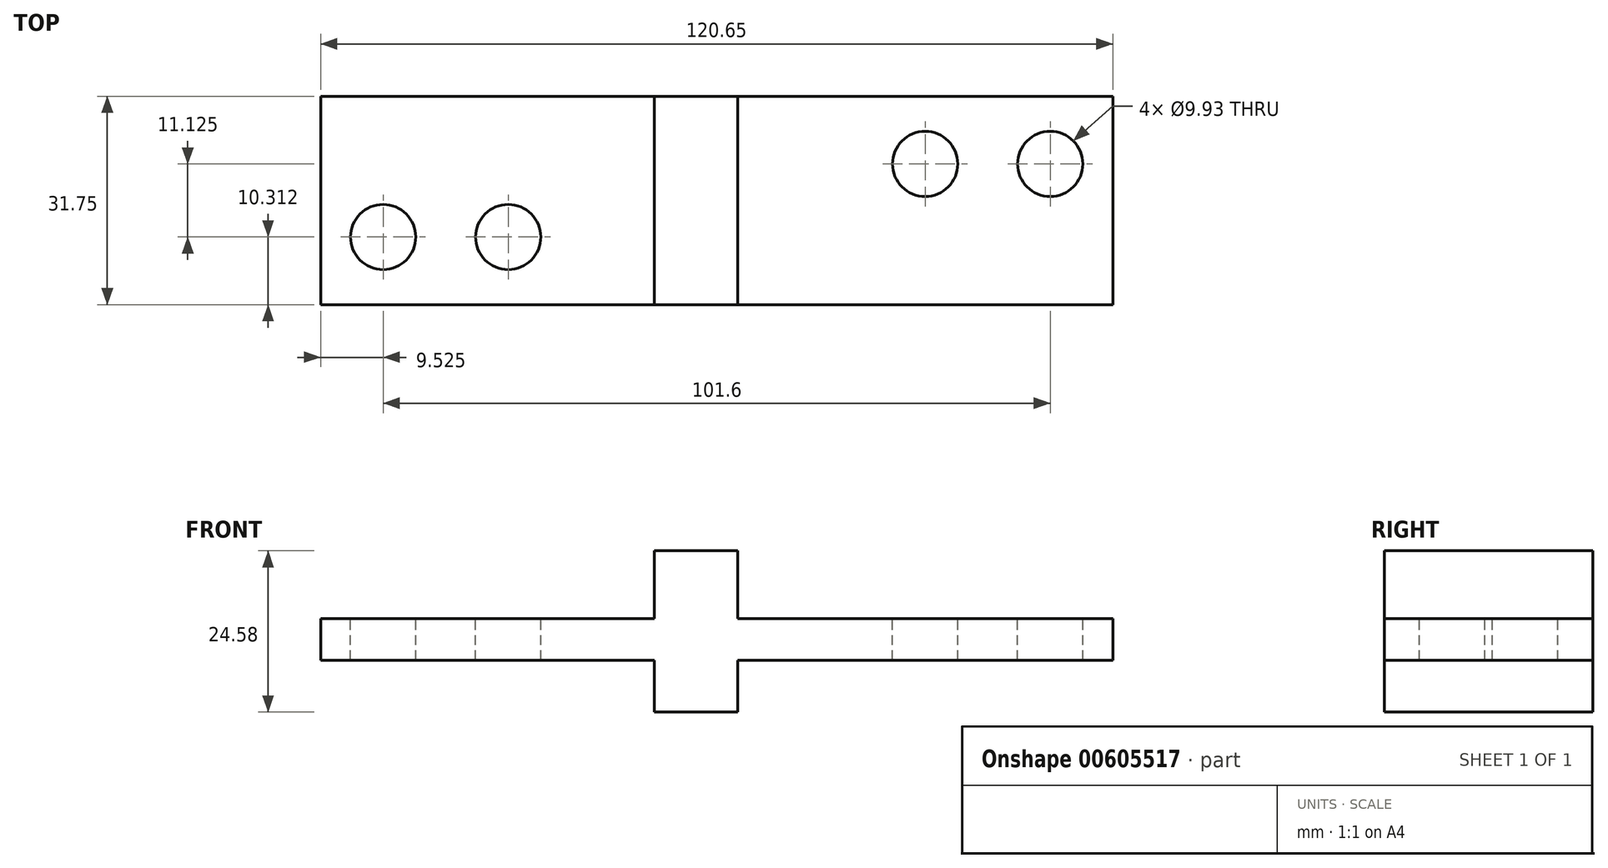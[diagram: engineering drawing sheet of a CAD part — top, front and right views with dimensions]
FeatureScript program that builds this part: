
annotation { "Feature Type Name" : "Feature", "Feature Type Description" : "" }
export const myFeature = defineFeature(function(context is Context, id is Id, definition is map)
    precondition{}
    {
        {
            var Q0;
            Q0=qCreatedBy(makeId("Front.planeOp"),FACE);
            var sketch = newSketch(context, id + "F0", { "sketchPlane" : qUnion([Q0])});
            skLineSegment(sketch, "E0", {"start": v(0, 0) * mm, "end": v(50.8, 0) * mm});
            skLineSegment(sketch, "E1", {"start": v(50.8, 0) * mm, "end": v(50.8, -7.92) * mm});
            skLineSegment(sketch, "E2", {"start": v(50.8, -7.92) * mm, "end": v(63.5, -7.92) * mm});
            skLineSegment(sketch, "E3", {"start": v(63.5, -7.92) * mm, "end": v(63.5, 0) * mm});
            skLineSegment(sketch, "E4", {"start": v(63.5, 0) * mm, "end": v(120.65, 0) * mm});
            skLineSegment(sketch, "E5", {"start": v(120.65, 0) * mm, "end": v(120.65, 6.35) * mm});
            skLineSegment(sketch, "E6", {"start": v(120.65, 6.35) * mm, "end": v(63.5, 6.35) * mm});
            skLineSegment(sketch, "E7", {"start": v(63.5, 6.35) * mm, "end": v(63.5, 16.66) * mm});
            skLineSegment(sketch, "E8", {"start": v(63.5, 16.66) * mm, "end": v(50.8, 16.66) * mm});
            skLineSegment(sketch, "E9", {"start": v(50.8, 16.66) * mm, "end": v(50.8, 6.35) * mm});
            skLineSegment(sketch, "E10", {"start": v(50.8, 6.35) * mm, "end": v(0, 6.35) * mm});
            skLineSegment(sketch, "E11", {"start": v(0, 6.35) * mm, "end": v(0, 0) * mm});
            skSolve(sketch);
        }
        {
            var Q0;
            Q0=makeQuery(id+"F0.imprint","IMPRINT",FACE,{"disambiguationData":[TD([[makeQuery(id+"F0.imprint","IMPRINT",EDGE,{"derivedFrom":sQuery(id+"F0.wireOp",EDGE,"E0")}),1.0]])]});
            extrude(context, id + "F1", {"entities" : qUnion([Q0]), "depth" : 31.75 * mm, "offsetDistance" : 25.4 * mm});
        }
        {
            var Q0;
            Q0=qCreatedBy(makeId("Top.planeOp"),FACE);
            var sketch = newSketch(context, id + "F2", { "sketchPlane" : qUnion([Q0])});
            skCircle(sketch, "E12", {"center": v(9.53, -21.44) * mm, "radius": 4.97 * mm});
            skCircle(sketch, "E13", {"center": v(28.57, -21.44) * mm, "radius": 4.97 * mm});
            skCircle(sketch, "E14", {"center": v(92.08, -10.31) * mm, "radius": 4.97 * mm});
            skCircle(sketch, "E15", {"center": v(111.12, -10.31) * mm, "radius": 4.97 * mm});
            skSolve(sketch);
        }
        {
            var Q0;
            Q0=sQuery(id+"F2.wireOp",VERTEX,"E15.center");
            var Q1;
            Q1=sQuery(id+"F2.wireOp",VERTEX,"E14.center");
            var Q2;
            Q2=sQuery(id+"F2.wireOp",VERTEX,"E13.center");
            var Q3;
            Q3=sQuery(id+"F2.wireOp",VERTEX,"E12.center");
            var Q4;
            Q4=makeQuery(id+"F1.opExtrude","SWEPT_BODY",BODY,{"disambiguationData":[OSD([sQuery(id+"F0.wireOp",EDGE,"E0"),sQuery(id+"F0.wireOp",EDGE,"E1"),sQuery(id+"F0.wireOp",EDGE,"E2"),sQuery(id+"F0.wireOp",EDGE,"E3"),sQuery(id+"F0.wireOp",EDGE,"E4"),sQuery(id+"F0.wireOp",EDGE,"E5"),sQuery(id+"F0.wireOp",EDGE,"E6"),sQuery(id+"F0.wireOp",EDGE,"E7"),sQuery(id+"F0.wireOp",EDGE,"E8"),sQuery(id+"F0.wireOp",EDGE,"E9"),sQuery(id+"F0.wireOp",EDGE,"E10"),sQuery(id+"F0.wireOp",EDGE,"E11")])]});
            hole(context, id + "F3", {"style" : HoleStyle.SIMPLE, "endStyle" : HoleEndStyle.THROUGH, "oppositeDirection" : true, "holeDiameter" : 9.93 * mm, "majorDiameter" : 6.35 * mm, "isTappedThrough" : true, "tappedDepth" : 12.7 * mm, "tapClearance" : 3, "locations" : qUnion([Q0, Q1, Q2, Q3]), "scope" : qUnion([Q4])});
        }
    });
